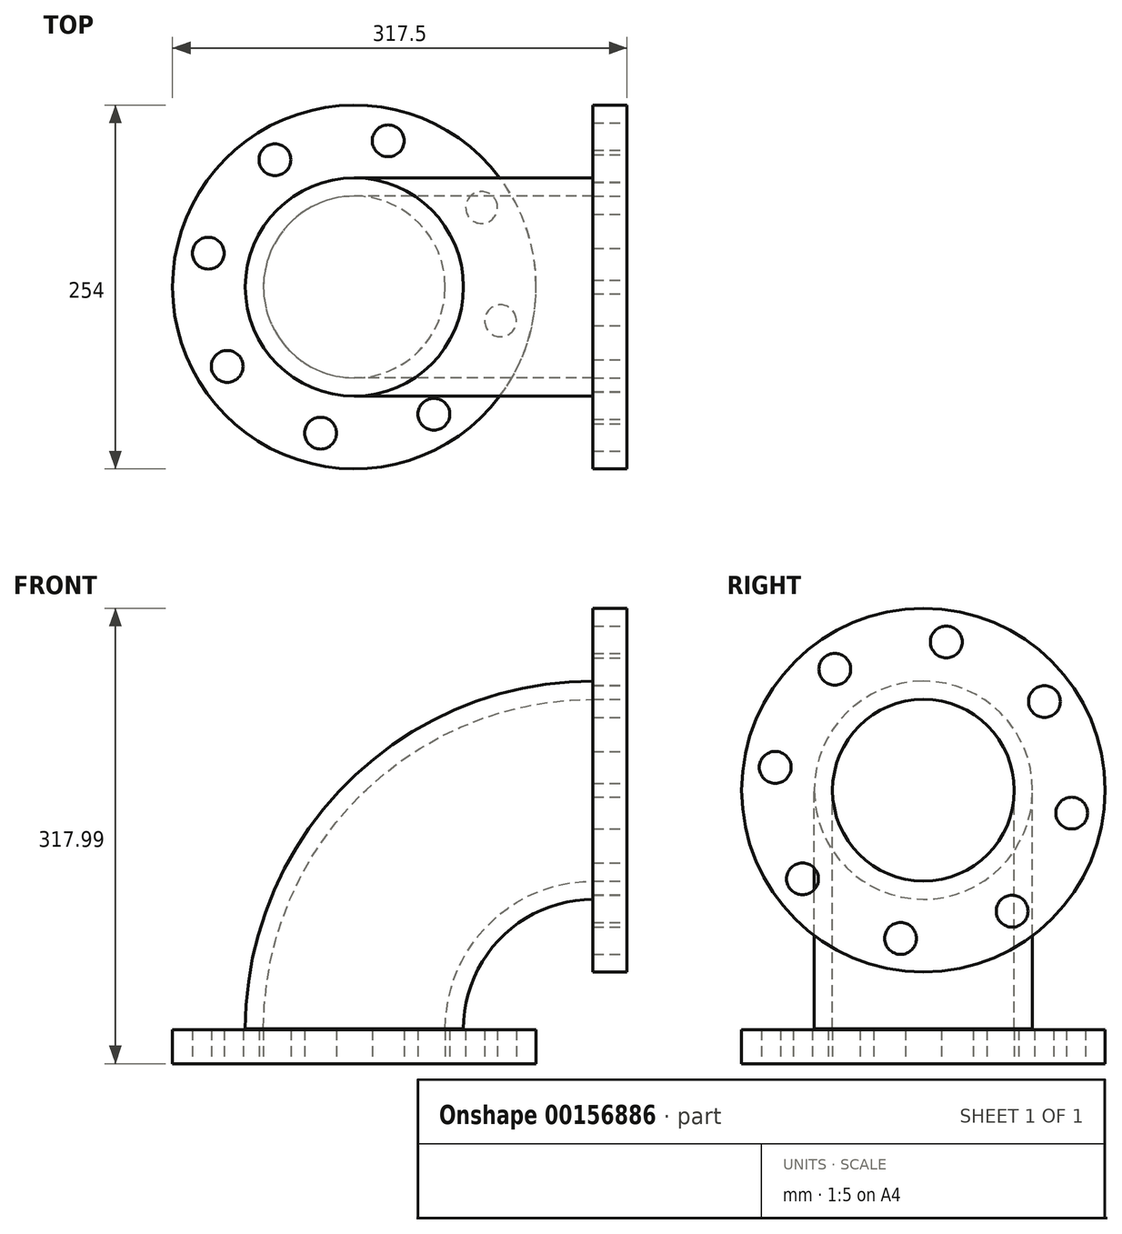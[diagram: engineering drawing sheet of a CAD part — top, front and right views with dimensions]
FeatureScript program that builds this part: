
annotation { "Feature Type Name" : "Feature", "Feature Type Description" : "" }
export const myFeature = defineFeature(function(context is Context, id is Id, definition is map)
    precondition{}
    {
        {
            var Q0;
            Q0=qCreatedBy(makeId("Top.planeOp"),FACE);
            var sketch = newSketch(context, id + "F0", { "sketchPlane" : qUnion([Q0])});
            skCircle(sketch, "E0", {"center": v(0, 0) * mm, "radius": 127 * mm});
            skCircle(sketch, "E1", {"center": v(-88.87, -55.5) * mm, "radius": 11.11 * mm});
            skCircle(sketch, "E2.1.0", {"center": v(-23.6, -102.08) * mm, "radius": 11.11 * mm});
            skCircle(sketch, "E2.2.0", {"center": v(55.5, -88.87) * mm, "radius": 11.11 * mm});
            skCircle(sketch, "E2.3.0", {"center": v(102.08, -23.6) * mm, "radius": 11.11 * mm});
            skCircle(sketch, "E2.4.0", {"center": v(88.87, 55.5) * mm, "radius": 11.11 * mm});
            skCircle(sketch, "E2.5.0", {"center": v(23.6, 102.08) * mm, "radius": 11.11 * mm});
            skCircle(sketch, "E2.6.0", {"center": v(-55.5, 88.87) * mm, "radius": 11.11 * mm});
            skCircle(sketch, "E2.7.0", {"center": v(-102.08, 23.6) * mm, "radius": 11.11 * mm});
            skCircle(sketch, "E3", {"center": v(0, 0) * mm, "radius": 63.5 * mm});
            skSolve(sketch);
        }
        {
            var Q0;
            Q0=qCreatedBy(makeId("Right.planeOp"),FACE);
            cPlane(context, id + "F1", {"entities" : qUnion([Q0]), "cplaneType" : CPlaneType.OFFSET, "offset" : 190.5 * mm, "width" : 152.4 * mm, "height" : 152.4 * mm});
        }
        {
            var Q0;
            Q0=qCreatedBy(id+"F1.planeOp",FACE);
            var sketch = newSketch(context, id + "F2", { "sketchPlane" : qUnion([Q0])});
            skCircle(sketch, "E4", {"center": v(0, 190.99) * mm, "radius": 127 * mm});
            skCircle(sketch, "E5", {"center": v(-61.93, 275.5) * mm, "radius": 11.11 * mm});
            skCircle(sketch, "E6.1.0", {"center": v(-103.55, 206.95) * mm, "radius": 11.11 * mm});
            skCircle(sketch, "E6.2.0", {"center": v(-84.51, 129.05) * mm, "radius": 11.11 * mm});
            skCircle(sketch, "E6.3.0", {"center": v(-15.97, 87.43) * mm, "radius": 11.11 * mm});
            skCircle(sketch, "E6.4.0", {"center": v(61.93, 106.47) * mm, "radius": 11.11 * mm});
            skCircle(sketch, "E6.5.0", {"center": v(103.55, 175.02) * mm, "radius": 11.11 * mm});
            skCircle(sketch, "E6.6.0", {"center": v(84.51, 252.92) * mm, "radius": 11.11 * mm});
            skCircle(sketch, "E6.7.0", {"center": v(15.97, 294.54) * mm, "radius": 11.11 * mm});
            skCircle(sketch, "E7", {"center": v(0, 190.99) * mm, "radius": 63.5 * mm});
            skSolve(sketch);
        }
        {
            var Q0;
            Q0=makeQuery(id+"F2.imprint","IMPRINT",FACE,{"disambiguationData":[TD([[makeQuery(id+"F2.imprint","IMPRINT",EDGE,{"derivedFrom":sQuery(id+"F2.wireOp",EDGE,"E4")}),1.0]])]});
            extrude(context, id + "F3", {"entities" : qUnion([Q0]), "oppositeDirection" : true, "depth" : 23.8 * mm});
        }
        {
            var Q0;
            Q0=makeQuery(id+"F3.opExtrude","CAP_FACE",FACE,{"disambiguationData":[OSD([sQuery(id+"F2.wireOp",EDGE,"E4"),sQuery(id+"F2.wireOp",EDGE,"E5"),sQuery(id+"F2.wireOp",EDGE,"E6.1.0"),sQuery(id+"F2.wireOp",EDGE,"E6.2.0"),sQuery(id+"F2.wireOp",EDGE,"E6.3.0"),sQuery(id+"F2.wireOp",EDGE,"E6.4.0"),sQuery(id+"F2.wireOp",EDGE,"E6.5.0"),sQuery(id+"F2.wireOp",EDGE,"E6.6.0"),sQuery(id+"F2.wireOp",EDGE,"E6.7.0"),sQuery(id+"F2.wireOp",EDGE,"E7")])],"isStart":false});
            var sketch = newSketch(context, id + "F4", { "sketchPlane" : qUnion([Q0])});
            skCircle(sketch, "E8", {"center": v(0, 190.99) * mm, "radius": 63.5 * mm});
            skCircle(sketch, "E9", {"center": v(0, 190.99) * mm, "radius": 76.2 * mm});
            skLineSegment(sketch, "E10", {"start": v(0, 190.99) * mm, "end": v(0, 24.3) * mm});
            skLineSegment(sketch, "E11", {"start": v(0, 24.3) * mm, "end": v(349.44, 24.3) * mm});
            skSolve(sketch);
        }
        {
            var Q0;
            Q0=makeQuery(id+"F4.imprint","IMPRINT",FACE,{"disambiguationData":[TD([[makeQuery(id+"F4.imprint","IMPRINT",EDGE,{"derivedFrom":sQuery(id+"F4.wireOp",EDGE,"E8")}),1.0]])]});
            var Q1;
            Q1=sQuery(id+"F4.wireOp",EDGE,"E11");
            revolve(context, id + "F5", {"operationType" : NewBodyOperationType.ADD, "entities" : qUnion([Q0]), "axis" : qUnion([Q1]), "revolveType" : RevolveType.ONE_DIRECTION, "angle" : 90 * degree});
        }
        {
            var Q0;
            Q0 = qSketchRegion(id + "F0", true);
            extrude(context, id + "F6", {"entities" : qUnion([Q0]), "depth" : 23.83 * mm});
        }
    });
